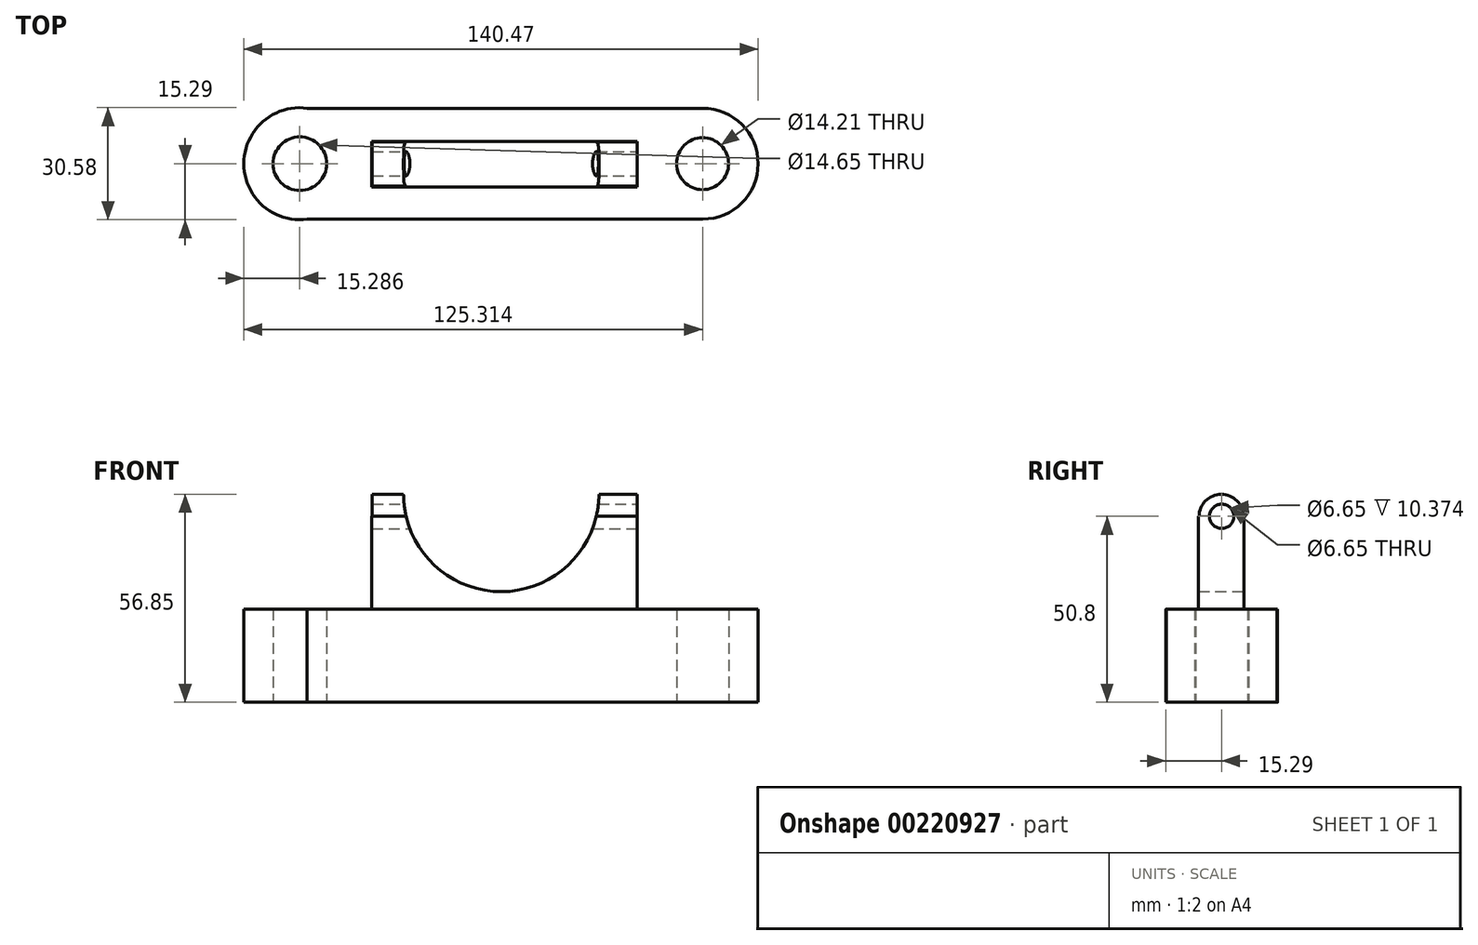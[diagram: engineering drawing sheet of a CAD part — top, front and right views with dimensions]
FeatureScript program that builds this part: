
annotation { "Feature Type Name" : "Feature", "Feature Type Description" : "" }
export const myFeature = defineFeature(function(context is Context, id is Id, definition is map)
    precondition{}
    {
        {
            var Q0;
            Q0=qCreatedBy(makeId("Top.planeOp"),FACE);
            var sketch = newSketch(context, id + "F0", { "sketchPlane" : qUnion([Q0])});
            skLineSegment(sketch, "E0.bottom", {"start": v(-55.01, 15.15) * mm, "end": v(55.01, 15.15) * mm});
            skLineSegment(sketch, "E0.top", {"start": v(-55.01, -15.15) * mm, "end": v(55.01, -15.15) * mm});
            skLineSegment(sketch, "E0.left", {"start": v(-55.01, 7.32) * mm, "end": v(-55.01, -7.32) * mm});
            skLineSegment(sketch, "E0.right", {"start": v(55.01, 7.1) * mm, "end": v(55.01, -7.1) * mm});
            skPoint(sketch, "E0.middle", {"position": v(0, 0) * mm});
            skArc(sketch, "E1", {"start": v(-53, 15.15) * mm, "mid": v(-70.3, 0) * mm, "end": v(-53, -15.15) * mm});
            skCircle(sketch, "E2", {"center": v(-55.01, 0) * mm, "radius": 7.32 * mm});
            skArc(sketch, "E3", {"start": v(55.01, -15.15) * mm, "mid": v(70.17, 0) * mm, "end": v(55.01, 15.15) * mm});
            skCircle(sketch, "E4", {"center": v(55.01, 0) * mm, "radius": 7.1 * mm});
            skSolve(sketch);
        }
        {
            var Q0;
            Q0 = qSketchRegion(id + "F0", true);
            extrude(context, id + "F1", {"entities" : qUnion([Q0]), "depth" : 25.4 * mm});
        }
        {
            var Q0;
            Q0=makeQuery(id+"F1.opExtrude","CAP_FACE",FACE,{"disambiguationData":[OSD([sQuery(id+"F0.wireOp",EDGE,"E0.bottom"),sQuery(id+"F0.wireOp",EDGE,"E0.top"),sQuery(id+"F0.wireOp",EDGE,"E1"),sQuery(id+"F0.wireOp",EDGE,"E2"),sQuery(id+"F0.wireOp",EDGE,"E3"),sQuery(id+"F0.wireOp",EDGE,"E4")])],"isStart":false});
            var sketch = newSketch(context, id + "F2", { "sketchPlane" : qUnion([Q0])});
            skLineSegment(sketch, "E5.bottom", {"start": v(-35.33, 6.12) * mm, "end": v(37.18, 6.12) * mm});
            skLineSegment(sketch, "E5.top", {"start": v(-35.33, -6.35) * mm, "end": v(37.18, -6.35) * mm});
            skLineSegment(sketch, "E5.left", {"start": v(-35.33, 6.12) * mm, "end": v(-35.33, -6.35) * mm});
            skLineSegment(sketch, "E5.right", {"start": v(37.18, 6.12) * mm, "end": v(37.18, -6.35) * mm});
            skSolve(sketch);
        }
        {
            var Q0;
            Q0 = qSketchRegion(id + "F2", true);
            extrude(context, id + "F3", {"entities" : qUnion([Q0]), "operationType" : NewBodyOperationType.ADD, "depth" : 25.4 * mm});
        }
        {
            var Q0;
            Q0=makeQuery(id+"F3.opExtrude","SWEPT_FACE",FACE,{"disambiguationData":[OSD([sQuery(id+"F2.wireOp",EDGE,"E5.right")])]});
            var sketch = newSketch(context, id + "F4", { "sketchPlane" : qUnion([Q0])});
            skCircle(sketch, "E6", {"center": v(-0.12, 50.8) * mm, "radius": 6.05 * mm});
            skCircle(sketch, "E7", {"center": v(-0.12, 50.8) * mm, "radius": 3.15 * mm});
            skSolve(sketch);
        }
        {
            var Q0;
            {var subQ0=sQuery(id+"F4.wireOp",EDGE,"E6");var subQ1=makeQuery(id+"F3.opExtrude","CAP_EDGE",EDGE,{"disambiguationData":[OSD([sQuery(id+"F2.wireOp",EDGE,"E5.right")])],"isStart":false});var subQ2=makeQuery(id+"F4.imprint","INTERSECT",VERTEX,{"disambiguationData":[OD(0.0)],"derivedFrom":[subQ1,subQ0]});Q0=makeQuery(id+"F4.imprint","IMPRINT",FACE,{"disambiguationData":[TD([[makeQuery(id+"F4.imprint","IMPRINT",EDGE,{"disambiguationData":[TD([[subQ2,-1.0]])],"derivedFrom":subQ0}),1.0]])]});}
            extrude(context, id + "F5", {"entities" : qUnion([Q0]), "operationType" : NewBodyOperationType.ADD, "oppositeDirection" : true, "depth" : 72.39 * mm});
        }
        {
            var Q0;
            {var subQ0=sQuery(id+"F2.wireOp",EDGE,"E5.right");Q0=makeQuery(id+"F5.boolean.opBoolean","MERGE",FACE,{"derivedFrom":[makeQuery(id+"F3.opExtrude","SWEPT_FACE",FACE,{"disambiguationData":[OSD([subQ0])]}),makeQuery(id+"F5.opExtrude","CAP_FACE",FACE,{"disambiguationData":[OSD([subQ0,sQuery(id+"F4.wireOp",EDGE,"E6"),sQuery(id+"F4.wireOp",EDGE,"E7")])],"isStart":true})]});}
            var sketch = newSketch(context, id + "F6", { "sketchPlane" : qUnion([Q0])});
            skCircle(sketch, "E8", {"center": v(0, 50.8) * mm, "radius": 3.32 * mm});
            skSolve(sketch);
        }
        {
            var Q0;
            Q0=makeQuery(id+"F6.imprint","IMPRINT",FACE,{"disambiguationData":[TD([[makeQuery(id+"F6.imprint","IMPRINT",EDGE,{"derivedFrom":sQuery(id+"F6.wireOp",EDGE,"E8")}),1.0]])]});
            var Q1;
            {var subQ0=sQuery(id+"F4.wireOp",EDGE,"E7");Q1=makeQuery(id+"F6.imprint","IMPRINT",FACE,{"disambiguationData":[TD([[makeQuery(id+"F6.imprint","IMPRINT",EDGE,{"derivedFrom":makeQuery(id+"F5.opExtrude","CAP_EDGE",EDGE,{"disambiguationData":[OSD([subQ0])],"isStart":true})}),1.0]])]});}
            extrude(context, id + "F7", {"entities" : qUnion([Q0, Q1]), "operationType" : NewBodyOperationType.REMOVE, "endBound" : BoundingType.THROUGH_ALL, "oppositeDirection" : true, "depth" : 25.4 * mm});
        }
        {
            var Q0;
            Q0=makeQuery(id+"F3.opExtrude","SWEPT_FACE",FACE,{"disambiguationData":[OSD([sQuery(id+"F2.wireOp",EDGE,"E5.bottom")])]});
            var sketch = newSketch(context, id + "F8", { "sketchPlane" : qUnion([Q0])});
            skCircle(sketch, "E9", {"center": v(0, 56.92) * mm, "radius": 26.68 * mm});
            skSolve(sketch);
        }
        {
            var Q0;
            {var subQ0=sQuery(id+"F8.wireOp",EDGE,"E9");var subQ1=makeQuery(id+"F3.opExtrude","CAP_EDGE",EDGE,{"disambiguationData":[OSD([sQuery(id+"F2.wireOp",EDGE,"E5.bottom")])],"isStart":false});var subQ2=makeQuery(id+"F8.imprint","INTERSECT",VERTEX,{"disambiguationData":[OD(0.0)],"derivedFrom":[subQ1,subQ0]});Q0=makeQuery(id+"F8.imprint","IMPRINT",FACE,{"disambiguationData":[TD([[makeQuery(id+"F8.imprint","IMPRINT",EDGE,{"disambiguationData":[TD([[subQ2,1.0]])],"derivedFrom":subQ0}),1.0]])]});}
            var Q1;
            {var subQ0=sQuery(id+"F8.wireOp",EDGE,"E9");var subQ1=makeQuery(id+"F3.opExtrude","CAP_EDGE",EDGE,{"disambiguationData":[OSD([sQuery(id+"F2.wireOp",EDGE,"E5.bottom")])],"isStart":false});var subQ2=makeQuery(id+"F8.imprint","INTERSECT",VERTEX,{"disambiguationData":[OD(0.0)],"derivedFrom":[subQ1,subQ0]});Q1=makeQuery(id+"F8.imprint","IMPRINT",FACE,{"disambiguationData":[TD([[makeQuery(id+"F8.imprint","IMPRINT",EDGE,{"disambiguationData":[TD([[subQ2,-1.0]])],"derivedFrom":subQ0}),1.0]])]});}
            extrude(context, id + "F9", {"entities" : qUnion([Q0, Q1]), "operationType" : NewBodyOperationType.REMOVE, "endBound" : BoundingType.THROUGH_ALL, "oppositeDirection" : true, "depth" : 25.4 * mm});
        }
    });
